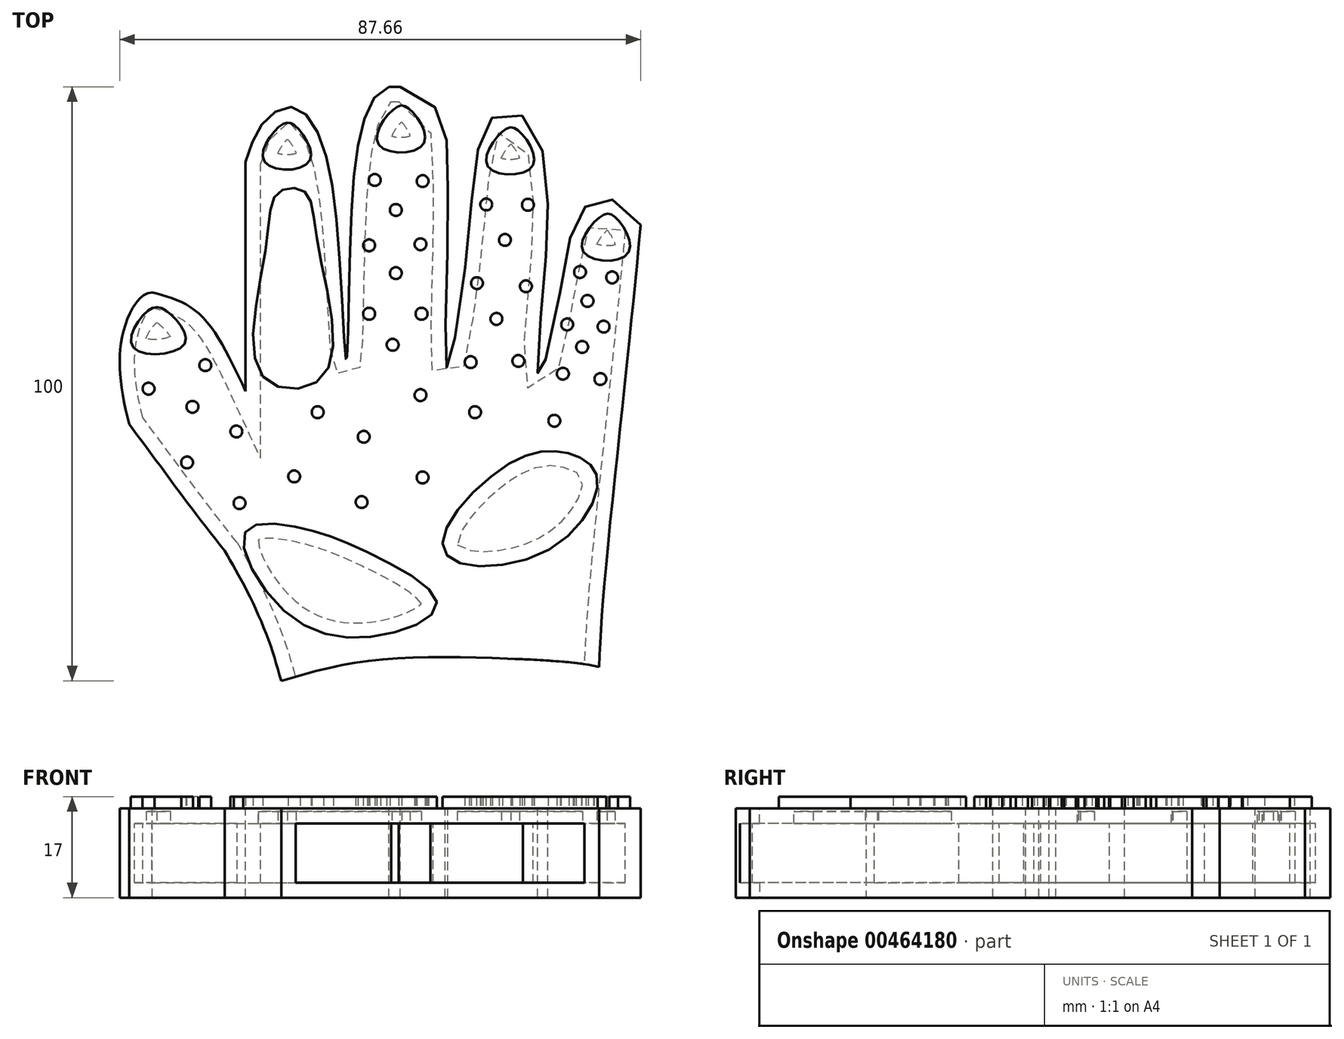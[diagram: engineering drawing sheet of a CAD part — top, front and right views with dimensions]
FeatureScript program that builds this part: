
annotation { "Feature Type Name" : "Feature", "Feature Type Description" : "" }
export const myFeature = defineFeature(function(context is Context, id is Id, definition is map)
    precondition{}
    {
        {
            var Q0;
            Q0=qCreatedBy(makeId("Top.planeOp"),FACE);
            var sketch = newSketch(context, id + "F0", { "sketchPlane" : qUnion([Q0])});
            skLineSegment(sketch, "E0.bottom", {"start": v(-33.1, 34.24) * mm, "end": v(36.9, 34.24) * mm});
            skLineSegment(sketch, "E0.top", {"start": v(-33.1, -40.76) * mm, "end": v(36.9, -40.76) * mm});
            skLineSegment(sketch, "E0.left", {"start": v(-33.1, 34.24) * mm, "end": v(-33.1, -40.76) * mm});
            skLineSegment(sketch, "E0.right", {"start": v(36.9, 34.24) * mm, "end": v(36.9, -40.76) * mm});
            skSolve(sketch);
        }
        {
            var Q0;
            Q0=makeQuery(id+"F0.imprint","IMPRINT",FACE,{"disambiguationData":[TD([[makeQuery(id+"F0.imprint","IMPRINT",EDGE,{"derivedFrom":sQuery(id+"F0.wireOp",EDGE,"E0.bottom")}),-1.0]])]});
            extrude(context, id + "F1", {"entities" : qUnion([Q0]), "depth" : 15 * mm});
        }
        {
            var Q0;
            Q0=makeQuery(id+"F1.opExtrude","SWEPT_FACE",FACE,{"disambiguationData":[OSD([sQuery(id+"F0.wireOp",EDGE,"E0.left")])]});
            var sketch = newSketch(context, id + "F2", { "sketchPlane" : qUnion([Q0])});
            skLineSegment(sketch, "E1.bottom", {"start": v(18.86, 15) * mm, "end": v(-24.65, 15) * mm});
            skLineSegment(sketch, "E1.top", {"start": v(18.86, 0) * mm, "end": v(-24.65, 0) * mm});
            skLineSegment(sketch, "E1.left", {"start": v(18.86, 15) * mm, "end": v(18.86, 0) * mm});
            skLineSegment(sketch, "E1.right", {"start": v(-24.65, 15) * mm, "end": v(-24.65, 0) * mm});
            skSolve(sketch);
        }
        {
            var Q0;
            Q0=makeQuery(id+"F2.imprint","IMPRINT",FACE,{"disambiguationData":[TD([[makeQuery(id+"F2.imprint","IMPRINT",EDGE,{"derivedFrom":sQuery(id+"F2.wireOp",EDGE,"E1.bottom")}),-1.0]])]});
            extrude(context, id + "F3", {"entities" : qUnion([Q0]), "operationType" : NewBodyOperationType.ADD, "depth" : 40 * mm});
        }
        {
            var Q0;
            Q0=makeQuery(id+"F3.boolean.opBoolean","MERGE",FACE,{"derivedFrom":[makeQuery(id+"F1.opExtrude","CAP_FACE",FACE,{"disambiguationData":[OSD([sQuery(id+"F0.wireOp",EDGE,"E0.bottom"),sQuery(id+"F0.wireOp",EDGE,"E0.top"),sQuery(id+"F0.wireOp",EDGE,"E0.left"),sQuery(id+"F0.wireOp",EDGE,"E0.right")])],"isStart":false}),makeQuery(id+"F3.opExtrude","SWEPT_FACE",FACE,{"disambiguationData":[OSD([sQuery(id+"F2.wireOp",EDGE,"E1.bottom")])]})]});
            var sketch = newSketch(context, id + "F4", { "sketchPlane" : qUnion([Q0])});
            skFitSpline(sketch, "E2", {"points": [v(-33.1, -18.86) * mm, v(-44.65, -8.02) * mm, v(-50.25, 7.45) * mm, v(-50.03, 18.49) * mm, v(-45.3, 24.65) * mm, v(-36.6, 18.45) * mm, v(-33.1, 13.36) * mm], "startDerivative": vector(-64.15, 47.66) * mm, "endDerivative": vector(21.3, -36.26) * mm});
            skFitSpline(sketch, "E3", {"points": [v(-33.1, 24.65) * mm, v(-33.1, 13.36) * mm], "startDerivative": vector(0, -11.29) * mm, "endDerivative": vector(0, -11.29) * mm});
            skSolve(sketch);
        }
        {
            var Q0;
            {var subQ2=sQuery(id+"F2.wireOp",EDGE,"E1.bottom");var subQ8=makeQuery(id+"F3.opExtrude","CAP_EDGE",EDGE,{"disambiguationData":[OSD([subQ2])],"isStart":false});Q0=makeQuery(id+"F4.imprint","IMPRINT",FACE,{"disambiguationData":[TD([[makeQuery(id+"F4.imprint","IMPRINT",EDGE,{"derivedFrom":subQ8}),1.0]])]});}
            extrude(context, id + "F5", {"entities" : qUnion([Q0]), "operationType" : NewBodyOperationType.REMOVE, "endBound" : BoundingType.THROUGH_ALL, "oppositeDirection" : true, "depth" : 25 * mm});
        }
        {
            var Q0;
            Q0=makeQuery(id+"F3.boolean.opBoolean","MERGE",FACE,{"derivedFrom":[makeQuery(id+"F1.opExtrude","CAP_FACE",FACE,{"disambiguationData":[OSD([sQuery(id+"F0.wireOp",EDGE,"E0.bottom"),sQuery(id+"F0.wireOp",EDGE,"E0.top"),sQuery(id+"F0.wireOp",EDGE,"E0.left"),sQuery(id+"F0.wireOp",EDGE,"E0.right")])],"isStart":false}),makeQuery(id+"F3.opExtrude","SWEPT_FACE",FACE,{"disambiguationData":[OSD([sQuery(id+"F2.wireOp",EDGE,"E1.bottom")])]})]});
            var sketch = newSketch(context, id + "F6", { "sketchPlane" : qUnion([Q0])});
            skFitSpline(sketch, "E4", {"points": [v(-45.3, 24.65) * mm, v(-37.58, 21.19) * mm, v(-29.58, 8) * mm], "startDerivative": vector(19.04, -4.98) * mm, "endDerivative": vector(12.7, -27.22) * mm});
            skLineSegment(sketch, "E5", {"start": v(-29.58, 8) * mm, "end": v(-29.58, 34.24) * mm});
            skSolve(sketch);
        }
        {
            var Q0;
            Q0=makeQuery(id+"F6.imprint","IMPRINT",FACE,{"disambiguationData":[TD([[makeQuery(id+"F6.imprint","IMPRINT",EDGE,{"derivedFrom":sQuery(id+"F6.wireOp",EDGE,"E4")}),1.0]])]});
            extrude(context, id + "F7", {"entities" : qUnion([Q0]), "operationType" : NewBodyOperationType.REMOVE, "endBound" : BoundingType.THROUGH_ALL, "oppositeDirection" : true, "depth" : 25 * mm});
        }
        {
            var Q0;
            Q0=makeQuery(id+"F3.boolean.opBoolean","MERGE",FACE,{"derivedFrom":[makeQuery(id+"F1.opExtrude","CAP_FACE",FACE,{"disambiguationData":[OSD([sQuery(id+"F0.wireOp",EDGE,"E0.bottom"),sQuery(id+"F0.wireOp",EDGE,"E0.top"),sQuery(id+"F0.wireOp",EDGE,"E0.left"),sQuery(id+"F0.wireOp",EDGE,"E0.right")])],"isStart":false}),makeQuery(id+"F3.opExtrude","SWEPT_FACE",FACE,{"disambiguationData":[OSD([sQuery(id+"F2.wireOp",EDGE,"E1.bottom")])]})]});
            var sketch = newSketch(context, id + "F8", { "sketchPlane" : qUnion([Q0])});
            skFitSpline(sketch, "E6", {"points": [v(-33.1, -18.86) * mm, v(-29.78, -24.78) * mm, v(-25.98, -33.18) * mm, v(-23.59, -40.76) * mm], "startDerivative": vector(10.61, -18.16) * mm, "endDerivative": vector(6.33, -22.3) * mm});
            skSolve(sketch);
        }
        {
            var Q0;
            {var subQ0=sQuery(id+"F8.wireOp",EDGE,"E6");Q0=makeQuery(id+"F8.imprint","IMPRINT",FACE,{"disambiguationData":[TD([[makeQuery(id+"F8.imprint","IMPRINT",EDGE,{"derivedFrom":subQ0}),-1.0]])]});}
            extrude(context, id + "F9", {"entities" : qUnion([Q0]), "operationType" : NewBodyOperationType.REMOVE, "endBound" : BoundingType.THROUGH_ALL, "oppositeDirection" : true, "depth" : 25 * mm});
        }
        {
            var Q0;
            Q0=makeQuery(id+"F3.boolean.opBoolean","MERGE",FACE,{"derivedFrom":[makeQuery(id+"F1.opExtrude","CAP_FACE",FACE,{"disambiguationData":[OSD([sQuery(id+"F0.wireOp",EDGE,"E0.bottom"),sQuery(id+"F0.wireOp",EDGE,"E0.top"),sQuery(id+"F0.wireOp",EDGE,"E0.left"),sQuery(id+"F0.wireOp",EDGE,"E0.right")])],"isStart":false}),makeQuery(id+"F3.opExtrude","SWEPT_FACE",FACE,{"disambiguationData":[OSD([sQuery(id+"F2.wireOp",EDGE,"E1.bottom")])]})]});
            var sketch = newSketch(context, id + "F10", { "sketchPlane" : qUnion([Q0])});
            skFitSpline(sketch, "E7", {"points": [v(-23.59, -40.76) * mm, v(-8.8, -37.38) * mm, v(13.4, -36.98) * mm, v(29.78, -38.38) * mm, v(36.9, -40.76) * mm], "startDerivative": vector(54.77, 16.06) * mm, "endDerivative": vector(35.94, -15) * mm});
            skSolve(sketch);
        }
        {
            var Q0;
            Q0=makeQuery(id+"F10.imprint","IMPRINT",FACE,{"disambiguationData":[TD([[makeQuery(id+"F10.imprint","IMPRINT",EDGE,{"derivedFrom":sQuery(id+"F10.wireOp",EDGE,"E7")}),-1.0]])]});
            extrude(context, id + "F11", {"entities" : qUnion([Q0]), "operationType" : NewBodyOperationType.REMOVE, "endBound" : BoundingType.THROUGH_ALL, "oppositeDirection" : true, "depth" : 25 * mm});
        }
        {
            var Q0;
            Q0=makeQuery(id+"F3.boolean.opBoolean","MERGE",FACE,{"derivedFrom":[makeQuery(id+"F1.opExtrude","CAP_FACE",FACE,{"disambiguationData":[OSD([sQuery(id+"F0.wireOp",EDGE,"E0.bottom"),sQuery(id+"F0.wireOp",EDGE,"E0.top"),sQuery(id+"F0.wireOp",EDGE,"E0.left"),sQuery(id+"F0.wireOp",EDGE,"E0.right")])],"isStart":false}),makeQuery(id+"F3.opExtrude","SWEPT_FACE",FACE,{"disambiguationData":[OSD([sQuery(id+"F2.wireOp",EDGE,"E1.bottom")])]})]});
            var sketch = newSketch(context, id + "F12", { "sketchPlane" : qUnion([Q0])});
            skFitSpline(sketch, "E8", {"points": [v(36.9, 6) * mm, v(34.98, -10.8) * mm, v(33.58, -28.98) * mm, v(32.48, -39.09) * mm], "startDerivative": vector(-5.85, -45.78) * mm, "endDerivative": vector(-4.13, -33.7) * mm});
            skSolve(sketch);
        }
        {
            var Q0;
            {var subQ0=sQuery(id+"F12.wireOp",EDGE,"E8");Q0=makeQuery(id+"F12.imprint","IMPRINT",FACE,{"disambiguationData":[TD([[makeQuery(id+"F12.imprint","IMPRINT",EDGE,{"derivedFrom":subQ0}),1.0]])]});}
            extrude(context, id + "F13", {"entities" : qUnion([Q0]), "operationType" : NewBodyOperationType.REMOVE, "endBound" : BoundingType.THROUGH_ALL, "oppositeDirection" : true, "depth" : 25 * mm});
        }
        {
            var Q0;
            Q0=makeQuery(id+"F1.opExtrude","SWEPT_FACE",FACE,{"disambiguationData":[OSD([sQuery(id+"F0.wireOp",EDGE,"E0.bottom")])]});
            var sketch = newSketch(context, id + "F14", { "sketchPlane" : qUnion([Q0])});
            skLineSegment(sketch, "E9.bottom", {"start": v(-36.9, 15) * mm, "end": v(29.58, 15) * mm});
            skLineSegment(sketch, "E9.top", {"start": v(-36.9, 0) * mm, "end": v(29.58, 0) * mm});
            skLineSegment(sketch, "E9.left", {"start": v(-36.9, 15) * mm, "end": v(-36.9, 0) * mm});
            skLineSegment(sketch, "E9.right", {"start": v(29.58, 15) * mm, "end": v(29.58, 0) * mm});
            skSolve(sketch);
        }
        {
            var Q0;
            Q0=makeQuery(id+"F14.imprint","IMPRINT",FACE,{"disambiguationData":[TD([[makeQuery(id+"F14.imprint","IMPRINT",EDGE,{"derivedFrom":sQuery(id+"F14.wireOp",EDGE,"E9.bottom")}),1.0]])]});
            extrude(context, id + "F15", {"entities" : qUnion([Q0]), "operationType" : NewBodyOperationType.ADD, "depth" : 25 * mm});
        }
        {
            var Q0;
            Q0=makeQuery(id+"F15.boolean.opBoolean","MERGE",FACE,{"derivedFrom":[makeQuery(id+"F3.boolean.opBoolean","MERGE",FACE,{"derivedFrom":[makeQuery(id+"F1.opExtrude","CAP_FACE",FACE,{"disambiguationData":[OSD([sQuery(id+"F0.wireOp",EDGE,"E0.bottom"),sQuery(id+"F0.wireOp",EDGE,"E0.top"),sQuery(id+"F0.wireOp",EDGE,"E0.left"),sQuery(id+"F0.wireOp",EDGE,"E0.right")])],"isStart":false}),makeQuery(id+"F3.opExtrude","SWEPT_FACE",FACE,{"disambiguationData":[OSD([sQuery(id+"F2.wireOp",EDGE,"E1.bottom")])]})]}),makeQuery(id+"F15.opExtrude","SWEPT_FACE",FACE,{"disambiguationData":[OSD([sQuery(id+"F14.wireOp",EDGE,"E9.bottom")])]})]});
            var sketch = newSketch(context, id + "F16", { "sketchPlane" : qUnion([Q0])});
            skFitSpline(sketch, "E10", {"points": [v(-29.58, 46.62) * mm, v(-26.4, 53.5) * mm, v(-21.52, 55.8) * mm, v(-16.93, 50.35) * mm, v(-13.77, 30.27) * mm, v(-12.62, 13.05) * mm, v(-12.05, 30.27) * mm, v(-10.04, 52.36) * mm, v(-5.45, 59.24) * mm, v(2.3, 55.8) * mm, v(4.3, 48.63) * mm, v(4.3, 27.68) * mm, v(4.3, 11.9) * mm, v(7.17, 27.4) * mm, v(9.47, 48.34) * mm, v(12.34, 54.36) * mm, v(17.79, 53.8) * mm, v(21.23, 41.17) * mm, v(20.37, 23.95) * mm, v(19.8, 10.18) * mm, v(23.81, 27.4) * mm, v(26.68, 38.01) * mm, v(30.98, 40.6) * mm, v(36.9, 36) * mm], "startDerivative": vector(69.6, 219.2) * mm, "endDerivative": vector(172.3, -192.55) * mm});
            skSolve(sketch);
        }
        {
            var Q0;
            {var subQ0=sQuery(id+"F16.wireOp",EDGE,"E10");var subQ1=sQuery(id+"F14.wireOp",EDGE,"E9.bottom");var subQ4=makeQuery(id+"F15.opExtrude","CAP_EDGE",EDGE,{"disambiguationData":[OSD([subQ1])],"isStart":false});var subQ5=makeQuery(id+"F16.imprint","INTERSECT",VERTEX,{"disambiguationData":[OD(1.0)],"derivedFrom":[subQ4,subQ0]});Q0=makeQuery(id+"F16.imprint","IMPRINT",FACE,{"disambiguationData":[TD([[makeQuery(id+"F16.imprint","IMPRINT",EDGE,{"disambiguationData":[TD([[subQ5,-1.0]])],"derivedFrom":subQ0}),1.0]])]});}
            var Q1;
            {var subQ0=sQuery(id+"F16.wireOp",EDGE,"E10");var subQ1=sQuery(id+"F14.wireOp",EDGE,"E9.bottom");var subQ4=makeQuery(id+"F15.opExtrude","CAP_EDGE",EDGE,{"disambiguationData":[OSD([subQ1])],"isStart":false});var subQ5=makeQuery(id+"F16.imprint","INTERSECT",VERTEX,{"disambiguationData":[OD(0.0)],"derivedFrom":[subQ4,subQ0]});Q1=makeQuery(id+"F16.imprint","IMPRINT",FACE,{"disambiguationData":[TD([[makeQuery(id+"F16.imprint","IMPRINT",EDGE,{"disambiguationData":[TD([[subQ5,1.0]])],"derivedFrom":subQ0}),1.0]])]});}
            extrude(context, id + "F17", {"entities" : qUnion([Q0, Q1]), "operationType" : NewBodyOperationType.REMOVE, "endBound" : BoundingType.THROUGH_ALL, "oppositeDirection" : true, "depth" : 25 * mm});
        }
        {
            var Q0;
            Q0=makeQuery(id+"F15.boolean.opBoolean","MERGE",FACE,{"derivedFrom":[makeQuery(id+"F3.boolean.opBoolean","MERGE",FACE,{"derivedFrom":[makeQuery(id+"F1.opExtrude","CAP_FACE",FACE,{"disambiguationData":[OSD([sQuery(id+"F0.wireOp",EDGE,"E0.bottom"),sQuery(id+"F0.wireOp",EDGE,"E0.top"),sQuery(id+"F0.wireOp",EDGE,"E0.left"),sQuery(id+"F0.wireOp",EDGE,"E0.right")])],"isStart":false}),makeQuery(id+"F3.opExtrude","SWEPT_FACE",FACE,{"disambiguationData":[OSD([sQuery(id+"F2.wireOp",EDGE,"E1.bottom")])]})]}),makeQuery(id+"F15.opExtrude","SWEPT_FACE",FACE,{"disambiguationData":[OSD([sQuery(id+"F14.wireOp",EDGE,"E9.bottom")])]})]});
            var sketch = newSketch(context, id + "F18", { "sketchPlane" : qUnion([Q0])});
            skFitSpline(sketch, "E11", {"points": [v(-33.1, -18.86) * mm, v(-39.6, -10.47) * mm, v(-44.47, -3.87) * mm, v(-49.17, 2.47) * mm], "startDerivative": vector(-18.5, 23.66) * mm, "endDerivative": vector(-14.92, 20.25) * mm});
            skSolve(sketch);
        }
        {
            var Q0;
            {var subQ0=sQuery(id+"F18.wireOp",EDGE,"E11");Q0=makeQuery(id+"F18.imprint","IMPRINT",FACE,{"disambiguationData":[TD([[makeQuery(id+"F18.imprint","IMPRINT",EDGE,{"derivedFrom":subQ0}),1.0]])]});}
            extrude(context, id + "F19", {"entities" : qUnion([Q0]), "operationType" : NewBodyOperationType.REMOVE, "endBound" : BoundingType.THROUGH_ALL, "oppositeDirection" : true, "depth" : 25 * mm});
        }
        {
            var Q0;
            Q0=makeQuery(id+"F15.boolean.opBoolean","MERGE",FACE,{"derivedFrom":[makeQuery(id+"F3.boolean.opBoolean","MERGE",FACE,{"derivedFrom":[makeQuery(id+"F1.opExtrude","CAP_FACE",FACE,{"disambiguationData":[OSD([sQuery(id+"F0.wireOp",EDGE,"E0.bottom"),sQuery(id+"F0.wireOp",EDGE,"E0.top"),sQuery(id+"F0.wireOp",EDGE,"E0.left"),sQuery(id+"F0.wireOp",EDGE,"E0.right")])],"isStart":false}),makeQuery(id+"F3.opExtrude","SWEPT_FACE",FACE,{"disambiguationData":[OSD([sQuery(id+"F2.wireOp",EDGE,"E1.bottom")])]})]}),makeQuery(id+"F15.opExtrude","SWEPT_FACE",FACE,{"disambiguationData":[OSD([sQuery(id+"F14.wireOp",EDGE,"E9.bottom")])]})]});
            var sketch = newSketch(context, id + "F20", { "sketchPlane" : qUnion([Q0])});
            skFitSpline(sketch, "E12", {"points": [v(36.9, 36) * mm, v(34.14, 8.46) * mm, v(30.7, -25.39) * mm, v(29.9, -38.4) * mm], "startDerivative": vector(-7.03, -72.25) * mm, "endDerivative": vector(-2.1, -45.84) * mm});
            skSolve(sketch);
        }
        {
            var Q0;
            {var subQ0=sQuery(id+"F20.wireOp",EDGE,"E12");Q0=makeQuery(id+"F20.imprint","IMPRINT",FACE,{"disambiguationData":[TD([[makeQuery(id+"F20.imprint","IMPRINT",EDGE,{"derivedFrom":subQ0}),1.0]])]});}
            extrude(context, id + "F21", {"entities" : qUnion([Q0]), "operationType" : NewBodyOperationType.REMOVE, "endBound" : BoundingType.THROUGH_ALL, "oppositeDirection" : true, "depth" : 25 * mm});
        }
        {
            var Q0;
            Q0=makeQuery(id+"F15.boolean.opBoolean","MERGE",FACE,{"derivedFrom":[makeQuery(id+"F3.boolean.opBoolean","MERGE",FACE,{"derivedFrom":[makeQuery(id+"F1.opExtrude","CAP_FACE",FACE,{"disambiguationData":[OSD([sQuery(id+"F0.wireOp",EDGE,"E0.bottom"),sQuery(id+"F0.wireOp",EDGE,"E0.top"),sQuery(id+"F0.wireOp",EDGE,"E0.left"),sQuery(id+"F0.wireOp",EDGE,"E0.right")])],"isStart":false}),makeQuery(id+"F3.opExtrude","SWEPT_FACE",FACE,{"disambiguationData":[OSD([sQuery(id+"F2.wireOp",EDGE,"E1.bottom")])]})]}),makeQuery(id+"F15.opExtrude","SWEPT_FACE",FACE,{"disambiguationData":[OSD([sQuery(id+"F14.wireOp",EDGE,"E9.bottom")])]})]});
            var sketch = newSketch(context, id + "F22", { "sketchPlane" : qUnion([Q0])});
            skFitSpline(sketch, "E13", {"points": [v(-26.4, 46.62) * mm, v(-23.81, 52.64) * mm, v(-21.23, 52.64) * mm, v(-18.93, 46.62) * mm, v(-26.4, 46.62) * mm]});
            skSolve(sketch);
        }
        {
            var Q0;
            Q0=makeQuery(id+"F22.imprint","IMPRINT",FACE,{"disambiguationData":[TD([[makeQuery(id+"F22.imprint","IMPRINT",EDGE,{"derivedFrom":sQuery(id+"F22.wireOp",EDGE,"E13")}),-1.0]])]});
            extrude(context, id + "F23", {"entities" : qUnion([Q0]), "operationType" : NewBodyOperationType.ADD, "depth" : 2 * mm});
        }
        {
            var Q0;
            Q0=makeQuery(id+"F15.boolean.opBoolean","MERGE",FACE,{"derivedFrom":[makeQuery(id+"F3.boolean.opBoolean","MERGE",FACE,{"derivedFrom":[makeQuery(id+"F1.opExtrude","CAP_FACE",FACE,{"disambiguationData":[OSD([sQuery(id+"F0.wireOp",EDGE,"E0.bottom"),sQuery(id+"F0.wireOp",EDGE,"E0.top"),sQuery(id+"F0.wireOp",EDGE,"E0.left"),sQuery(id+"F0.wireOp",EDGE,"E0.right")])],"isStart":false}),makeQuery(id+"F3.opExtrude","SWEPT_FACE",FACE,{"disambiguationData":[OSD([sQuery(id+"F2.wireOp",EDGE,"E1.bottom")])]})]}),makeQuery(id+"F15.opExtrude","SWEPT_FACE",FACE,{"disambiguationData":[OSD([sQuery(id+"F14.wireOp",EDGE,"E9.bottom")])]})]});
            var sketch = newSketch(context, id + "F24", { "sketchPlane" : qUnion([Q0])});
            skFitSpline(sketch, "E14", {"points": [v(-7.2, 49.52) * mm, v(-4.62, 55.54) * mm, v(-2.04, 55.54) * mm, v(0.26, 49.52) * mm, v(-7.2, 49.52) * mm]});
            skSolve(sketch);
        }
        {
            var Q0;
            Q0=makeQuery(id+"F24.imprint","IMPRINT",FACE,{"disambiguationData":[TD([[makeQuery(id+"F24.imprint","IMPRINT",EDGE,{"derivedFrom":sQuery(id+"F24.wireOp",EDGE,"E14")}),-1.0]])]});
            extrude(context, id + "F25", {"entities" : qUnion([Q0]), "operationType" : NewBodyOperationType.ADD, "depth" : 2 * mm});
        }
        {
            var Q0;
            Q0=makeQuery(id+"F15.boolean.opBoolean","MERGE",FACE,{"derivedFrom":[makeQuery(id+"F3.boolean.opBoolean","MERGE",FACE,{"derivedFrom":[makeQuery(id+"F1.opExtrude","CAP_FACE",FACE,{"disambiguationData":[OSD([sQuery(id+"F0.wireOp",EDGE,"E0.bottom"),sQuery(id+"F0.wireOp",EDGE,"E0.top"),sQuery(id+"F0.wireOp",EDGE,"E0.left"),sQuery(id+"F0.wireOp",EDGE,"E0.right")])],"isStart":false}),makeQuery(id+"F3.opExtrude","SWEPT_FACE",FACE,{"disambiguationData":[OSD([sQuery(id+"F2.wireOp",EDGE,"E1.bottom")])]})]}),makeQuery(id+"F15.opExtrude","SWEPT_FACE",FACE,{"disambiguationData":[OSD([sQuery(id+"F14.wireOp",EDGE,"E9.bottom")])]})]});
            var sketch = newSketch(context, id + "F26", { "sketchPlane" : qUnion([Q0])});
            skFitSpline(sketch, "E15", {"points": [v(11.2, 45.82) * mm, v(13.77, 51.84) * mm, v(16.35, 51.84) * mm, v(18.65, 45.82) * mm, v(11.2, 45.82) * mm]});
            skSolve(sketch);
        }
        {
            var Q0;
            Q0=makeQuery(id+"F26.imprint","IMPRINT",FACE,{"disambiguationData":[TD([[makeQuery(id+"F26.imprint","IMPRINT",EDGE,{"derivedFrom":sQuery(id+"F26.wireOp",EDGE,"E15")}),-1.0]])]});
            extrude(context, id + "F27", {"entities" : qUnion([Q0]), "operationType" : NewBodyOperationType.ADD, "depth" : 2 * mm});
        }
        {
            var Q0;
            Q0=makeQuery(id+"F15.boolean.opBoolean","MERGE",FACE,{"derivedFrom":[makeQuery(id+"F3.boolean.opBoolean","MERGE",FACE,{"derivedFrom":[makeQuery(id+"F1.opExtrude","CAP_FACE",FACE,{"disambiguationData":[OSD([sQuery(id+"F0.wireOp",EDGE,"E0.bottom"),sQuery(id+"F0.wireOp",EDGE,"E0.top"),sQuery(id+"F0.wireOp",EDGE,"E0.left"),sQuery(id+"F0.wireOp",EDGE,"E0.right")])],"isStart":false}),makeQuery(id+"F3.opExtrude","SWEPT_FACE",FACE,{"disambiguationData":[OSD([sQuery(id+"F2.wireOp",EDGE,"E1.bottom")])]})]}),makeQuery(id+"F15.opExtrude","SWEPT_FACE",FACE,{"disambiguationData":[OSD([sQuery(id+"F14.wireOp",EDGE,"E9.bottom")])]})]});
            var sketch = newSketch(context, id + "F28", { "sketchPlane" : qUnion([Q0])});
            skFitSpline(sketch, "E16", {"points": [v(27.22, 31.48) * mm, v(30.08, 37.37) * mm, v(32.66, 37.25) * mm, v(34.67, 31.13) * mm, v(27.22, 31.48) * mm]});
            skSolve(sketch);
        }
        {
            var Q0;
            Q0=makeQuery(id+"F28.imprint","IMPRINT",FACE,{"disambiguationData":[TD([[makeQuery(id+"F28.imprint","IMPRINT",EDGE,{"derivedFrom":sQuery(id+"F28.wireOp",EDGE,"E16")}),-1.0]])]});
            extrude(context, id + "F29", {"entities" : qUnion([Q0]), "operationType" : NewBodyOperationType.ADD, "depth" : 2 * mm});
        }
        {
            var Q0;
            Q0=makeQuery(id+"F15.boolean.opBoolean","MERGE",FACE,{"derivedFrom":[makeQuery(id+"F3.boolean.opBoolean","MERGE",FACE,{"derivedFrom":[makeQuery(id+"F1.opExtrude","CAP_FACE",FACE,{"disambiguationData":[OSD([sQuery(id+"F0.wireOp",EDGE,"E0.bottom"),sQuery(id+"F0.wireOp",EDGE,"E0.top"),sQuery(id+"F0.wireOp",EDGE,"E0.left"),sQuery(id+"F0.wireOp",EDGE,"E0.right")])],"isStart":false}),makeQuery(id+"F3.opExtrude","SWEPT_FACE",FACE,{"disambiguationData":[OSD([sQuery(id+"F2.wireOp",EDGE,"E1.bottom")])]})]}),makeQuery(id+"F15.opExtrude","SWEPT_FACE",FACE,{"disambiguationData":[OSD([sQuery(id+"F14.wireOp",EDGE,"E9.bottom")])]})]});
            var sketch = newSketch(context, id + "F30", { "sketchPlane" : qUnion([Q0])});
            skFitSpline(sketch, "E17", {"points": [v(-48.48, 15.35) * mm, v(-45.9, 21.66) * mm, v(-42.75, 21.37) * mm, v(-39.88, 15.92) * mm, v(-48.48, 15.35) * mm]});
            skSolve(sketch);
        }
        {
            var Q0;
            Q0=makeQuery(id+"F30.imprint","IMPRINT",FACE,{"disambiguationData":[TD([[makeQuery(id+"F30.imprint","IMPRINT",EDGE,{"derivedFrom":sQuery(id+"F30.wireOp",EDGE,"E17")}),-1.0]])]});
            extrude(context, id + "F31", {"entities" : qUnion([Q0]), "operationType" : NewBodyOperationType.ADD, "depth" : 2 * mm});
        }
        {
            var Q0;
            Q0=makeQuery(id+"F15.boolean.opBoolean","MERGE",FACE,{"derivedFrom":[makeQuery(id+"F3.boolean.opBoolean","MERGE",FACE,{"derivedFrom":[makeQuery(id+"F1.opExtrude","CAP_FACE",FACE,{"disambiguationData":[OSD([sQuery(id+"F0.wireOp",EDGE,"E0.bottom"),sQuery(id+"F0.wireOp",EDGE,"E0.top"),sQuery(id+"F0.wireOp",EDGE,"E0.left"),sQuery(id+"F0.wireOp",EDGE,"E0.right")])],"isStart":false}),makeQuery(id+"F3.opExtrude","SWEPT_FACE",FACE,{"disambiguationData":[OSD([sQuery(id+"F2.wireOp",EDGE,"E1.bottom")])]})]}),makeQuery(id+"F15.opExtrude","SWEPT_FACE",FACE,{"disambiguationData":[OSD([sQuery(id+"F14.wireOp",EDGE,"E9.bottom")])]})]});
            var sketch = newSketch(context, id + "F32", { "sketchPlane" : qUnion([Q0])});
            skFitSpline(sketch, "E18", {"points": [v(-9.18, -19.08) * mm, v(-20.08, -15.06) * mm, v(-29.58, -15.64) * mm, v(-22.95, -29.12) * mm, v(-6.89, -33.14) * mm, v(2.58, -27.68) * mm, v(-9.18, -19.08) * mm]});
            skFitSpline(sketch, "E19", {"points": [v(24.67, -2.44) * mm, v(14.34, -4.45) * mm, v(3.73, -18.8) * mm, v(20.66, -19.08) * mm, v(29.55, -6.45) * mm, v(24.67, -2.44) * mm]});
            skSolve(sketch);
        }
        {
            var Q0;
            Q0=makeQuery(id+"F32.imprint","IMPRINT",FACE,{"disambiguationData":[TD([[makeQuery(id+"F32.imprint","IMPRINT",EDGE,{"derivedFrom":sQuery(id+"F32.wireOp",EDGE,"E18")}),1.0]])]});
            var Q1;
            Q1=makeQuery(id+"F32.imprint","IMPRINT",FACE,{"disambiguationData":[TD([[makeQuery(id+"F32.imprint","IMPRINT",EDGE,{"derivedFrom":sQuery(id+"F32.wireOp",EDGE,"E19")}),1.0]])]});
            extrude(context, id + "F33", {"entities" : qUnion([Q0, Q1]), "operationType" : NewBodyOperationType.ADD, "depth" : 2 * mm});
        }
        {
            var Q0;
            Q0=makeQuery(id+"F15.boolean.opBoolean","MERGE",FACE,{"derivedFrom":[makeQuery(id+"F3.boolean.opBoolean","MERGE",FACE,{"derivedFrom":[makeQuery(id+"F1.opExtrude","CAP_FACE",FACE,{"disambiguationData":[OSD([sQuery(id+"F0.wireOp",EDGE,"E0.bottom"),sQuery(id+"F0.wireOp",EDGE,"E0.top"),sQuery(id+"F0.wireOp",EDGE,"E0.left"),sQuery(id+"F0.wireOp",EDGE,"E0.right")])],"isStart":false}),makeQuery(id+"F3.opExtrude","SWEPT_FACE",FACE,{"disambiguationData":[OSD([sQuery(id+"F2.wireOp",EDGE,"E1.bottom")])]})]}),makeQuery(id+"F15.opExtrude","SWEPT_FACE",FACE,{"disambiguationData":[OSD([sQuery(id+"F14.wireOp",EDGE,"E9.bottom")])]})]});
            var sketch = newSketch(context, id + "F34", { "sketchPlane" : qUnion([Q0])});
            skFitSpline(sketch, "E20", {"points": [v(-26.68, 10.47) * mm, v(-26.1, 32.56) * mm, v(-24.1, 41.45) * mm, v(-19.8, 41.74) * mm, v(-17.5, 33.14) * mm, v(-16.35, 10.76) * mm, v(-26.68, 10.47) * mm]});
            skSolve(sketch);
        }
        {
            var Q0;
            Q0=makeQuery(id+"F34.imprint","IMPRINT",FACE,{"disambiguationData":[TD([[makeQuery(id+"F34.imprint","IMPRINT",EDGE,{"derivedFrom":sQuery(id+"F34.wireOp",EDGE,"E20")}),-1.0]])]});
            extrude(context, id + "F35", {"entities" : qUnion([Q0]), "operationType" : NewBodyOperationType.ADD, "depth" : 2 * mm});
        }
        {
            var Q0;
            Q0=makeQuery(id+"F15.boolean.opBoolean","MERGE",FACE,{"derivedFrom":[makeQuery(id+"F3.boolean.opBoolean","MERGE",FACE,{"derivedFrom":[makeQuery(id+"F1.opExtrude","CAP_FACE",FACE,{"disambiguationData":[OSD([sQuery(id+"F0.wireOp",EDGE,"E0.bottom"),sQuery(id+"F0.wireOp",EDGE,"E0.top"),sQuery(id+"F0.wireOp",EDGE,"E0.left"),sQuery(id+"F0.wireOp",EDGE,"E0.right")])],"isStart":false}),makeQuery(id+"F3.opExtrude","SWEPT_FACE",FACE,{"disambiguationData":[OSD([sQuery(id+"F2.wireOp",EDGE,"E1.bottom")])]})]}),makeQuery(id+"F15.opExtrude","SWEPT_FACE",FACE,{"disambiguationData":[OSD([sQuery(id+"F14.wireOp",EDGE,"E9.bottom")])]})]});
            var sketch = newSketch(context, id + "F36", { "sketchPlane" : qUnion([Q0])});
            skCircle(sketch, "E21", {"center": v(10.9, 39.45) * mm, "radius": 1 * mm});
            skCircle(sketch, "E22", {"center": v(17.92, 39.4) * mm, "radius": 1 * mm});
            skCircle(sketch, "E23", {"center": v(14.05, 33.48) * mm, "radius": 1 * mm});
            skCircle(sketch, "E24", {"center": v(9.34, 26.2) * mm, "radius": 1 * mm});
            skCircle(sketch, "E25", {"center": v(17.58, 25.67) * mm, "radius": 1 * mm});
            skCircle(sketch, "E26", {"center": v(12.62, 20.18) * mm, "radius": 1 * mm});
            skCircle(sketch, "E27", {"center": v(8.29, 12.9) * mm, "radius": 1 * mm});
            skCircle(sketch, "E28", {"center": v(16.31, 13.1) * mm, "radius": 1 * mm});
            skSolve(sketch);
        }
        {
            var Q0;
            Q0=makeQuery(id+"F36.imprint","IMPRINT",FACE,{"disambiguationData":[TD([[makeQuery(id+"F36.imprint","IMPRINT",EDGE,{"derivedFrom":sQuery(id+"F36.wireOp",EDGE,"E21")}),1.0]])]});
            var Q1;
            Q1=makeQuery(id+"F36.imprint","IMPRINT",FACE,{"disambiguationData":[TD([[makeQuery(id+"F36.imprint","IMPRINT",EDGE,{"derivedFrom":sQuery(id+"F36.wireOp",EDGE,"E22")}),1.0]])]});
            var Q2;
            Q2=makeQuery(id+"F36.imprint","IMPRINT",FACE,{"disambiguationData":[TD([[makeQuery(id+"F36.imprint","IMPRINT",EDGE,{"derivedFrom":sQuery(id+"F36.wireOp",EDGE,"E23")}),1.0]])]});
            var Q3;
            Q3=makeQuery(id+"F36.imprint","IMPRINT",FACE,{"disambiguationData":[TD([[makeQuery(id+"F36.imprint","IMPRINT",EDGE,{"derivedFrom":sQuery(id+"F36.wireOp",EDGE,"E25")}),1.0]])]});
            var Q4;
            Q4=makeQuery(id+"F36.imprint","IMPRINT",FACE,{"disambiguationData":[TD([[makeQuery(id+"F36.imprint","IMPRINT",EDGE,{"derivedFrom":sQuery(id+"F36.wireOp",EDGE,"E24")}),1.0]])]});
            var Q5;
            Q5=makeQuery(id+"F36.imprint","IMPRINT",FACE,{"disambiguationData":[TD([[makeQuery(id+"F36.imprint","IMPRINT",EDGE,{"derivedFrom":sQuery(id+"F36.wireOp",EDGE,"E26")}),1.0]])]});
            var Q6;
            Q6=makeQuery(id+"F36.imprint","IMPRINT",FACE,{"disambiguationData":[TD([[makeQuery(id+"F36.imprint","IMPRINT",EDGE,{"derivedFrom":sQuery(id+"F36.wireOp",EDGE,"E28")}),1.0]])]});
            var Q7;
            Q7=makeQuery(id+"F36.imprint","IMPRINT",FACE,{"disambiguationData":[TD([[makeQuery(id+"F36.imprint","IMPRINT",EDGE,{"derivedFrom":sQuery(id+"F36.wireOp",EDGE,"E27")}),1.0]])]});
            extrude(context, id + "F37", {"entities" : qUnion([Q0, Q1, Q2, Q3, Q4, Q5, Q6, Q7]), "operationType" : NewBodyOperationType.ADD, "depth" : 2 * mm});
        }
        {
            var Q0;
            Q0=makeQuery(id+"F15.boolean.opBoolean","MERGE",FACE,{"derivedFrom":[makeQuery(id+"F3.boolean.opBoolean","MERGE",FACE,{"derivedFrom":[makeQuery(id+"F1.opExtrude","CAP_FACE",FACE,{"disambiguationData":[OSD([sQuery(id+"F0.wireOp",EDGE,"E0.bottom"),sQuery(id+"F0.wireOp",EDGE,"E0.top"),sQuery(id+"F0.wireOp",EDGE,"E0.left"),sQuery(id+"F0.wireOp",EDGE,"E0.right")])],"isStart":false}),makeQuery(id+"F3.opExtrude","SWEPT_FACE",FACE,{"disambiguationData":[OSD([sQuery(id+"F2.wireOp",EDGE,"E1.bottom")])]})]}),makeQuery(id+"F15.opExtrude","SWEPT_FACE",FACE,{"disambiguationData":[OSD([sQuery(id+"F14.wireOp",EDGE,"E9.bottom")])]})]});
            var sketch = newSketch(context, id + "F38", { "sketchPlane" : qUnion([Q0])});
            skCircle(sketch, "E29", {"center": v(-7.85, 43.57) * mm, "radius": 1 * mm});
            skCircle(sketch, "E30", {"center": v(0.2, 43.38) * mm, "radius": 1 * mm});
            skCircle(sketch, "E31", {"center": v(-4.3, 38.51) * mm, "radius": 1 * mm});
            skCircle(sketch, "E32", {"center": v(-8.8, 32.57) * mm, "radius": 1 * mm});
            skCircle(sketch, "E33", {"center": v(-0.16, 32.75) * mm, "radius": 1 * mm});
            skCircle(sketch, "E34", {"center": v(-4.3, 27.89) * mm, "radius": 1 * mm});
            skCircle(sketch, "E35", {"center": v(-8.8, 21.04) * mm, "radius": 1 * mm});
            skCircle(sketch, "E36", {"center": v(0.02, 21.04) * mm, "radius": 1 * mm});
            skCircle(sketch, "E37", {"center": v(-4.84, 15.82) * mm, "radius": 1 * mm});
            skCircle(sketch, "E38", {"center": v(26.68, 28.07) * mm, "radius": 1 * mm});
            skCircle(sketch, "E39", {"center": v(32.08, 27.16) * mm, "radius": 1 * mm});
            skCircle(sketch, "E40", {"center": v(27.94, 23.2) * mm, "radius": 1 * mm});
            skCircle(sketch, "E41", {"center": v(30.64, 18.88) * mm, "radius": 1 * mm});
            skCircle(sketch, "E42", {"center": v(24.52, 19.24) * mm, "radius": 1 * mm});
            skCircle(sketch, "E43", {"center": v(27.04, 15.46) * mm, "radius": 1 * mm});
            skCircle(sketch, "E44", {"center": v(30.1, 10.05) * mm, "radius": 1 * mm});
            skCircle(sketch, "E45", {"center": v(23.8, 10.95) * mm, "radius": 1 * mm});
            skCircle(sketch, "E46", {"center": v(-36.36, 12.4) * mm, "radius": 1 * mm});
            skCircle(sketch, "E47", {"center": v(-45.9, 8.43) * mm, "radius": 1 * mm});
            skCircle(sketch, "E48", {"center": v(-38.52, 5.37) * mm, "radius": 1 * mm});
            skCircle(sketch, "E49", {"center": v(-39.42, -4) * mm, "radius": 1 * mm});
            skCircle(sketch, "E50", {"center": v(-31.14, 1.23) * mm, "radius": 1 * mm});
            skCircle(sketch, "E51", {"center": v(-17.45, 4.47) * mm, "radius": 1 * mm});
            skCircle(sketch, "E52", {"center": v(-21.41, -6.34) * mm, "radius": 1 * mm});
            skCircle(sketch, "E53", {"center": v(-30.6, -10.84) * mm, "radius": 1 * mm});
            skCircle(sketch, "E54", {"center": v(-9.7, 0.33) * mm, "radius": 1 * mm});
            skCircle(sketch, "E55", {"center": v(-10.06, -10.66) * mm, "radius": 1 * mm});
            skCircle(sketch, "E56", {"center": v(9.03, 4.47) * mm, "radius": 1 * mm});
            skCircle(sketch, "E57", {"center": v(22.36, 3.03) * mm, "radius": 1 * mm});
            skCircle(sketch, "E58", {"center": v(0.2, -6.52) * mm, "radius": 1 * mm});
            skCircle(sketch, "E59", {"center": v(-0.16, 7.35) * mm, "radius": 1 * mm});
            skSolve(sketch);
        }
        {
            var Q0;
            Q0=makeQuery(id+"F38.imprint","IMPRINT",FACE,{"disambiguationData":[TD([[makeQuery(id+"F38.imprint","IMPRINT",EDGE,{"derivedFrom":sQuery(id+"F38.wireOp",EDGE,"E29")}),1.0]])]});
            var Q1;
            Q1=makeQuery(id+"F38.imprint","IMPRINT",FACE,{"disambiguationData":[TD([[makeQuery(id+"F38.imprint","IMPRINT",EDGE,{"derivedFrom":sQuery(id+"F38.wireOp",EDGE,"E31")}),1.0]])]});
            var Q2;
            Q2=makeQuery(id+"F38.imprint","IMPRINT",FACE,{"disambiguationData":[TD([[makeQuery(id+"F38.imprint","IMPRINT",EDGE,{"derivedFrom":sQuery(id+"F38.wireOp",EDGE,"E30")}),1.0]])]});
            var Q3;
            Q3=makeQuery(id+"F38.imprint","IMPRINT",FACE,{"disambiguationData":[TD([[makeQuery(id+"F38.imprint","IMPRINT",EDGE,{"derivedFrom":sQuery(id+"F38.wireOp",EDGE,"E33")}),1.0]])]});
            var Q4;
            Q4=makeQuery(id+"F38.imprint","IMPRINT",FACE,{"disambiguationData":[TD([[makeQuery(id+"F38.imprint","IMPRINT",EDGE,{"derivedFrom":sQuery(id+"F38.wireOp",EDGE,"E32")}),1.0]])]});
            var Q5;
            Q5=makeQuery(id+"F38.imprint","IMPRINT",FACE,{"disambiguationData":[TD([[makeQuery(id+"F38.imprint","IMPRINT",EDGE,{"derivedFrom":sQuery(id+"F38.wireOp",EDGE,"E34")}),1.0]])]});
            var Q6;
            Q6=makeQuery(id+"F38.imprint","IMPRINT",FACE,{"disambiguationData":[TD([[makeQuery(id+"F38.imprint","IMPRINT",EDGE,{"derivedFrom":sQuery(id+"F38.wireOp",EDGE,"E36")}),1.0]])]});
            var Q7;
            Q7=makeQuery(id+"F38.imprint","IMPRINT",FACE,{"disambiguationData":[TD([[makeQuery(id+"F38.imprint","IMPRINT",EDGE,{"derivedFrom":sQuery(id+"F38.wireOp",EDGE,"E35")}),1.0]])]});
            var Q8;
            Q8=makeQuery(id+"F38.imprint","IMPRINT",FACE,{"disambiguationData":[TD([[makeQuery(id+"F38.imprint","IMPRINT",EDGE,{"derivedFrom":sQuery(id+"F38.wireOp",EDGE,"E37")}),1.0]])]});
            var Q9;
            Q9=makeQuery(id+"F38.imprint","IMPRINT",FACE,{"disambiguationData":[TD([[makeQuery(id+"F38.imprint","IMPRINT",EDGE,{"derivedFrom":sQuery(id+"F38.wireOp",EDGE,"E38")}),1.0]])]});
            var Q10;
            Q10=makeQuery(id+"F38.imprint","IMPRINT",FACE,{"disambiguationData":[TD([[makeQuery(id+"F38.imprint","IMPRINT",EDGE,{"derivedFrom":sQuery(id+"F38.wireOp",EDGE,"E39")}),1.0]])]});
            var Q11;
            Q11=makeQuery(id+"F38.imprint","IMPRINT",FACE,{"disambiguationData":[TD([[makeQuery(id+"F38.imprint","IMPRINT",EDGE,{"derivedFrom":sQuery(id+"F38.wireOp",EDGE,"E40")}),1.0]])]});
            var Q12;
            Q12=makeQuery(id+"F38.imprint","IMPRINT",FACE,{"disambiguationData":[TD([[makeQuery(id+"F38.imprint","IMPRINT",EDGE,{"derivedFrom":sQuery(id+"F38.wireOp",EDGE,"E42")}),1.0]])]});
            var Q13;
            Q13=makeQuery(id+"F38.imprint","IMPRINT",FACE,{"disambiguationData":[TD([[makeQuery(id+"F38.imprint","IMPRINT",EDGE,{"derivedFrom":sQuery(id+"F38.wireOp",EDGE,"E43")}),1.0]])]});
            var Q14;
            Q14=makeQuery(id+"F38.imprint","IMPRINT",FACE,{"disambiguationData":[TD([[makeQuery(id+"F38.imprint","IMPRINT",EDGE,{"derivedFrom":sQuery(id+"F38.wireOp",EDGE,"E41")}),1.0]])]});
            var Q15;
            Q15=makeQuery(id+"F38.imprint","IMPRINT",FACE,{"disambiguationData":[TD([[makeQuery(id+"F38.imprint","IMPRINT",EDGE,{"derivedFrom":sQuery(id+"F38.wireOp",EDGE,"E44")}),1.0]])]});
            var Q16;
            Q16=makeQuery(id+"F38.imprint","IMPRINT",FACE,{"disambiguationData":[TD([[makeQuery(id+"F38.imprint","IMPRINT",EDGE,{"derivedFrom":sQuery(id+"F38.wireOp",EDGE,"E45")}),1.0]])]});
            var Q17;
            Q17=makeQuery(id+"F38.imprint","IMPRINT",FACE,{"disambiguationData":[TD([[makeQuery(id+"F38.imprint","IMPRINT",EDGE,{"derivedFrom":sQuery(id+"F38.wireOp",EDGE,"E47")}),1.0]])]});
            var Q18;
            Q18=makeQuery(id+"F38.imprint","IMPRINT",FACE,{"disambiguationData":[TD([[makeQuery(id+"F38.imprint","IMPRINT",EDGE,{"derivedFrom":sQuery(id+"F38.wireOp",EDGE,"E50")}),1.0]])]});
            var Q19;
            Q19=makeQuery(id+"F38.imprint","IMPRINT",FACE,{"disambiguationData":[TD([[makeQuery(id+"F38.imprint","IMPRINT",EDGE,{"derivedFrom":sQuery(id+"F38.wireOp",EDGE,"E49")}),1.0]])]});
            var Q20;
            Q20=makeQuery(id+"F38.imprint","IMPRINT",FACE,{"disambiguationData":[TD([[makeQuery(id+"F38.imprint","IMPRINT",EDGE,{"derivedFrom":sQuery(id+"F38.wireOp",EDGE,"E51")}),1.0]])]});
            var Q21;
            Q21=makeQuery(id+"F38.imprint","IMPRINT",FACE,{"disambiguationData":[TD([[makeQuery(id+"F38.imprint","IMPRINT",EDGE,{"derivedFrom":sQuery(id+"F38.wireOp",EDGE,"E48")}),1.0]])]});
            var Q22;
            Q22=makeQuery(id+"F38.imprint","IMPRINT",FACE,{"disambiguationData":[TD([[makeQuery(id+"F38.imprint","IMPRINT",EDGE,{"derivedFrom":sQuery(id+"F38.wireOp",EDGE,"E46")}),1.0]])]});
            var Q23;
            Q23=makeQuery(id+"F38.imprint","IMPRINT",FACE,{"disambiguationData":[TD([[makeQuery(id+"F38.imprint","IMPRINT",EDGE,{"derivedFrom":sQuery(id+"F38.wireOp",EDGE,"E59")}),1.0]])]});
            var Q24;
            Q24=makeQuery(id+"F38.imprint","IMPRINT",FACE,{"disambiguationData":[TD([[makeQuery(id+"F38.imprint","IMPRINT",EDGE,{"derivedFrom":sQuery(id+"F38.wireOp",EDGE,"E56")}),1.0]])]});
            var Q25;
            Q25=makeQuery(id+"F38.imprint","IMPRINT",FACE,{"disambiguationData":[TD([[makeQuery(id+"F38.imprint","IMPRINT",EDGE,{"derivedFrom":sQuery(id+"F38.wireOp",EDGE,"E57")}),1.0]])]});
            var Q26;
            Q26=makeQuery(id+"F38.imprint","IMPRINT",FACE,{"disambiguationData":[TD([[makeQuery(id+"F38.imprint","IMPRINT",EDGE,{"derivedFrom":sQuery(id+"F38.wireOp",EDGE,"E58")}),1.0]])]});
            var Q27;
            Q27=makeQuery(id+"F38.imprint","IMPRINT",FACE,{"disambiguationData":[TD([[makeQuery(id+"F38.imprint","IMPRINT",EDGE,{"derivedFrom":sQuery(id+"F38.wireOp",EDGE,"E54")}),1.0]])]});
            var Q28;
            Q28=makeQuery(id+"F38.imprint","IMPRINT",FACE,{"disambiguationData":[TD([[makeQuery(id+"F38.imprint","IMPRINT",EDGE,{"derivedFrom":sQuery(id+"F38.wireOp",EDGE,"E52")}),1.0]])]});
            var Q29;
            Q29=makeQuery(id+"F38.imprint","IMPRINT",FACE,{"disambiguationData":[TD([[makeQuery(id+"F38.imprint","IMPRINT",EDGE,{"derivedFrom":sQuery(id+"F38.wireOp",EDGE,"E55")}),1.0]])]});
            var Q30;
            Q30=makeQuery(id+"F38.imprint","IMPRINT",FACE,{"disambiguationData":[TD([[makeQuery(id+"F38.imprint","IMPRINT",EDGE,{"derivedFrom":sQuery(id+"F38.wireOp",EDGE,"E53")}),1.0]])]});
            extrude(context, id + "F39", {"entities" : qUnion([Q0, Q1, Q2, Q3, Q4, Q5, Q6, Q7, Q8, Q9, Q10, Q11, Q12, Q13, Q14, Q15, Q16, Q17, Q18, Q19, Q20, Q21, Q22, Q23, Q24, Q25, Q26, Q27, Q28, Q29, Q30]), "operationType" : NewBodyOperationType.ADD, "depth" : 2 * mm});
        }
        {
            var Q0;
            Q0=makeQuery(id+"F11.boolean.opBoolean","COPY",FACE,{"derivedFrom":makeQuery(id+"F11.opExtrude","SWEPT_FACE",FACE,{"disambiguationData":[OSD([sQuery(id+"F10.wireOp",EDGE,"E7")])]})});
            shell(context, id + "F40", {"entities" : qUnion([Q0]), "thickness" : 2.5 * mm});
        }
    });
